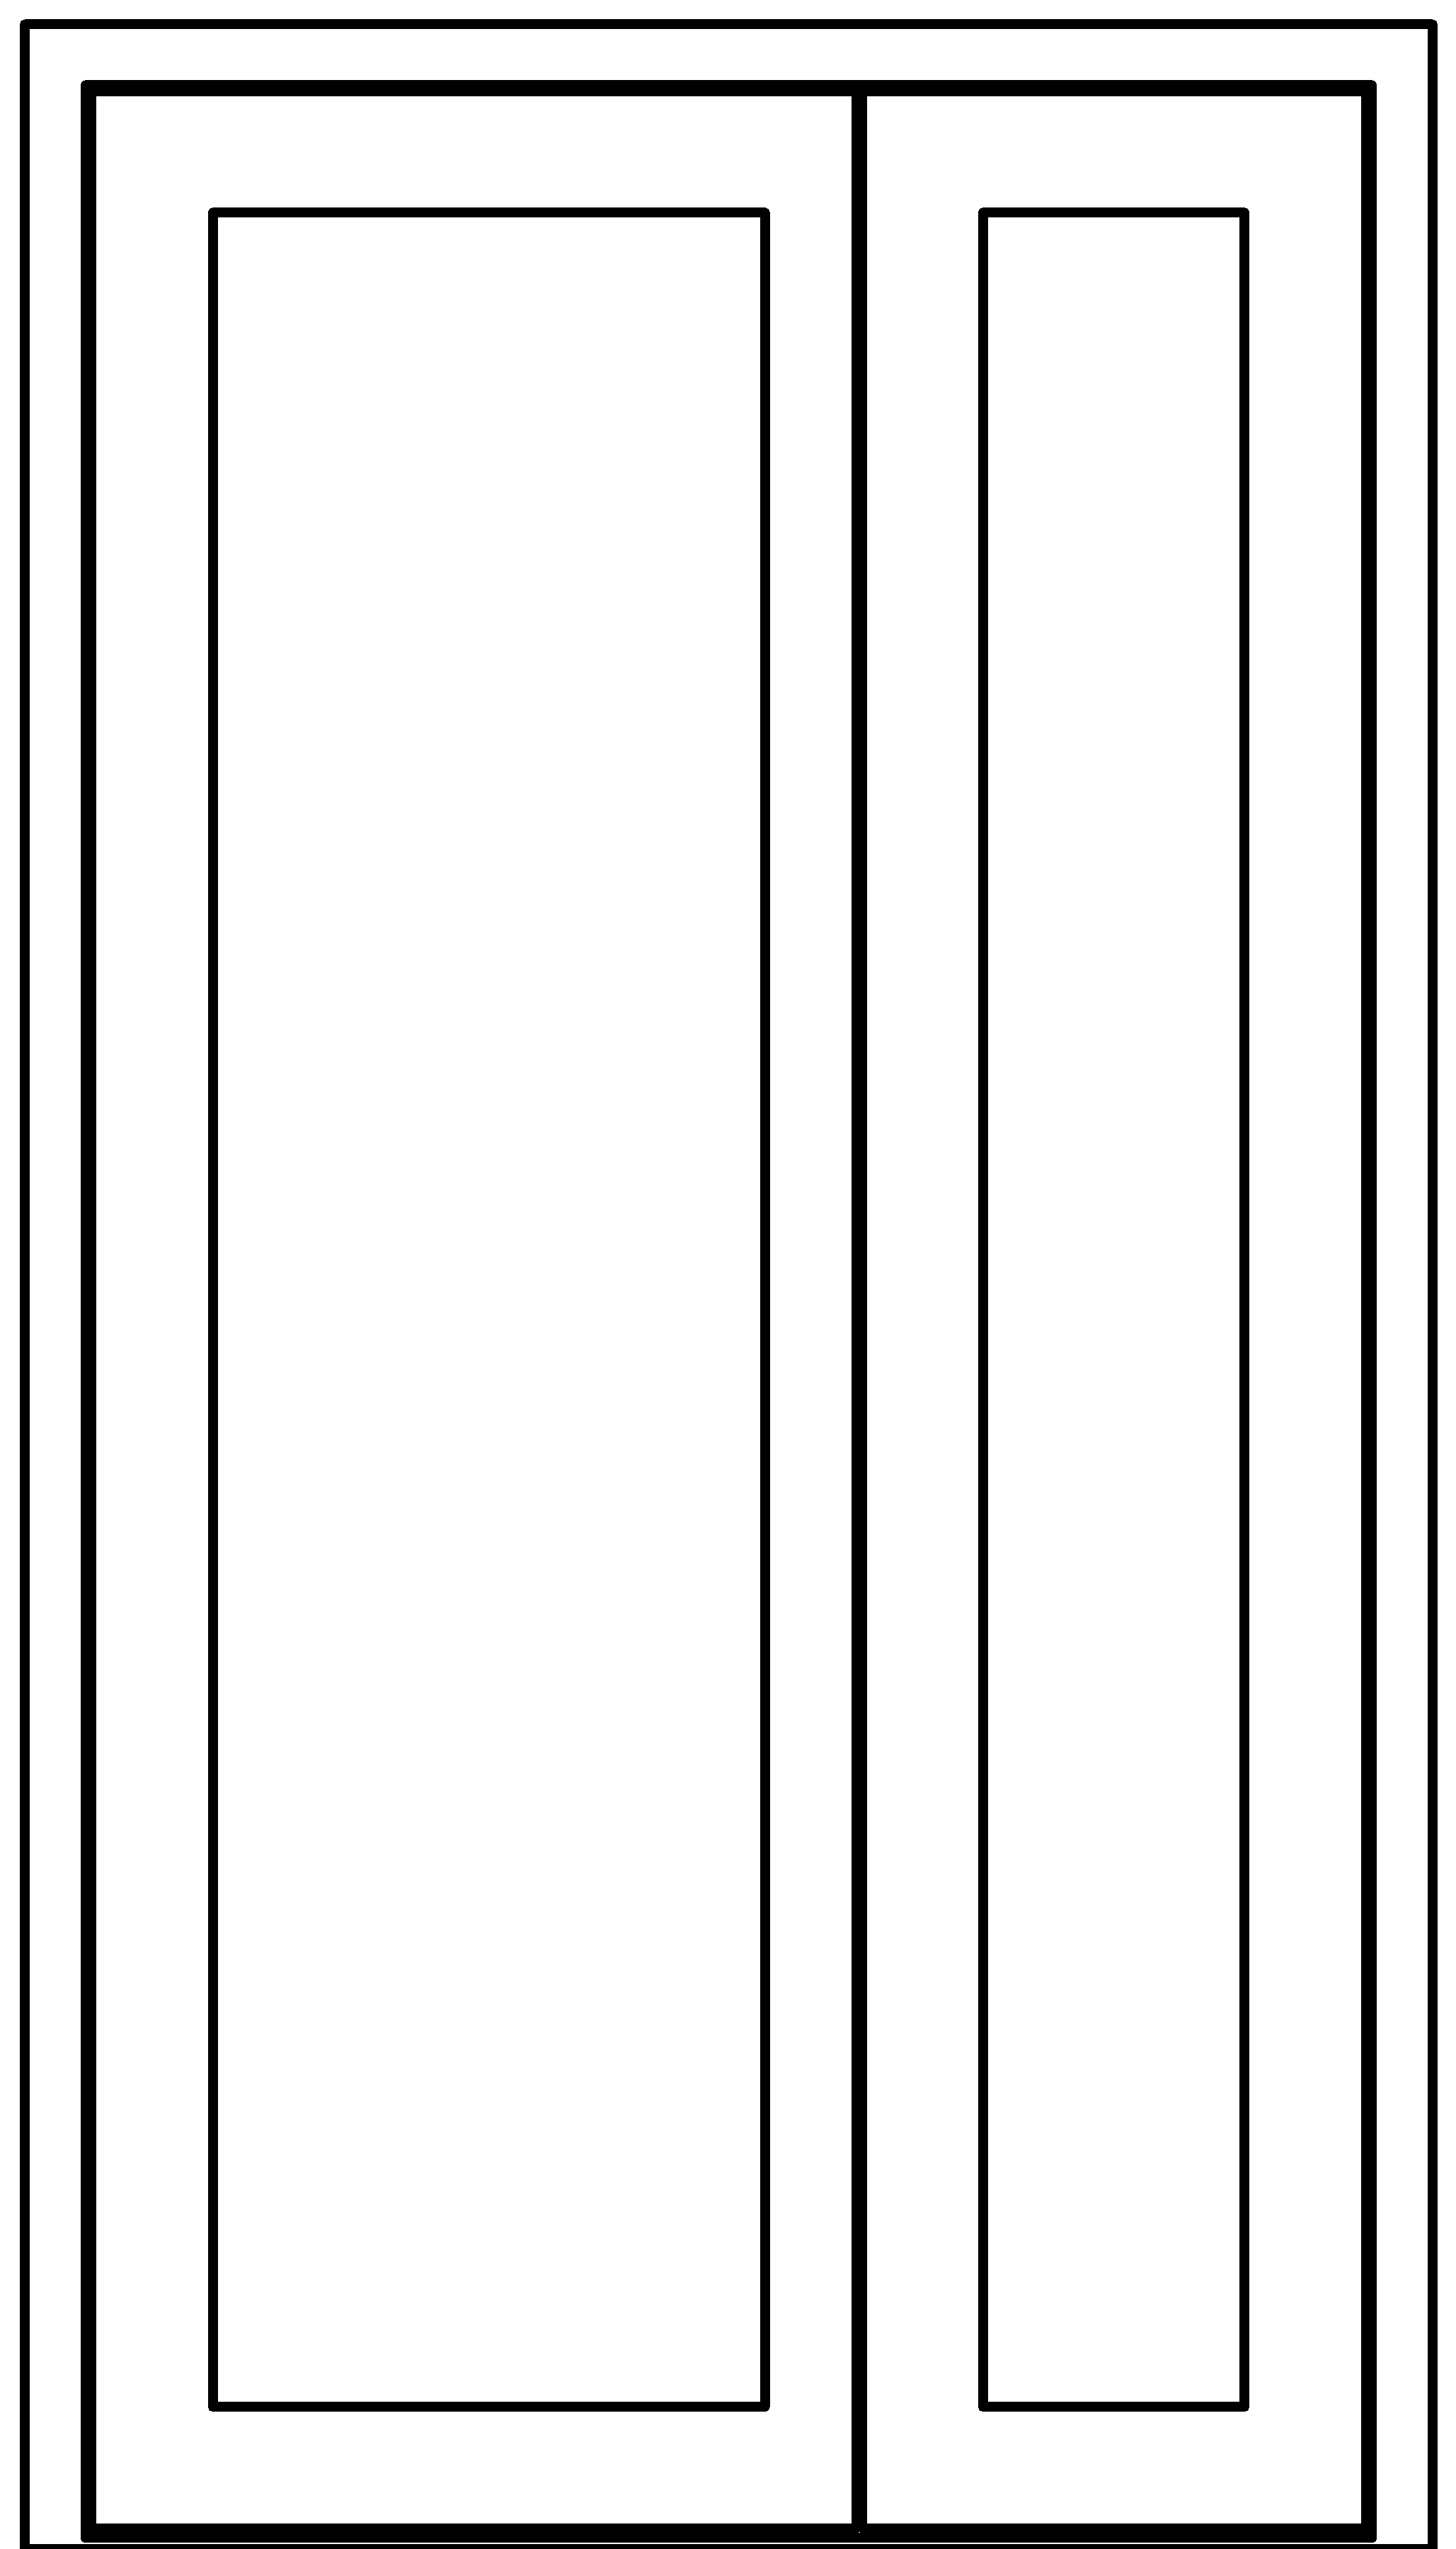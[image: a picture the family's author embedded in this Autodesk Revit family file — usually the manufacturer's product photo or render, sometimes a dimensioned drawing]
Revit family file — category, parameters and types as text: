
# Revit family: Дверь.Alumark_двупольная_S40
name_source: partatom
category: Двери
revit_build: Autodesk Revit 2017 (Build: 20171027_0315(x64)
units: mm (PartAtom-declared; Revit-internal decimal feet)

## family parameters
Всегда вертикально = Да
Заголовок OmniClass = Doors
Номер OmniClass = 23.30.10.00
Общий = Нет
Основа = Стена
При загрузке вырезать с полостями = Нет
Точка расчета площади = Нет

## types (2) — shared parameters
ADSK_Завод-изготовитель = ТБМ
ADSK_Обозначение = ГОСТ 23747-2015
URL = http://www.tbm.ru
sp_energy = Энергосберегающие стекла
sp_gaz = Заполненный газом
sp_standart = Обычный стеклопакет
Аналитическая конструкция = Застеклённая створчатая дверь, металлическая рама с двумя стеклами
Высота импоста = 800 мм
Дверь с цоколем = Нет
Заполнение стеклопакета = Обычный стеклопакет
Изготовитель = ТБМ
Изображение типоразмера = схема_двупольная_дверь.png
Импост двери = Нет
Коэффициент теплопередачи (U) = 4.2812 Вт/(м²·K)
Материал остекления = <По категории>
Материал профилей = <По категории>
Материал фурнитуры = <По категории>
Одинаковые полотна = Да
Описание = Дверь Проем ТБМ
Примерная высота = 2080 мм
Примерная ширина = 1160 мм
Разработчик = ООО ПРОРУБИМ
Разработчик (телефон) = +7(495)649-85-43
ТБМ_Артикул_Крепление порога = ALM740630
ТБМ_Артикул_Подкладка под СП = ALM740307
ТБМ_Артикул_Порог = ALM240391
ТБМ_Артикул_Рама = ALM240180
ТБМ_Артикул_Распорный штифт = ALM885014
ТБМ_Артикул_Т-соединитель рамы = ALM740322
ТБМ_Артикул_Угловой соединитель рамы = ALM740508
ТБМ_Артикул_Угловой соединитель створки = ALM740509
ТБМ_Артикул_Уголок выравнивающий = ALM740011
ТБМ_Артикул_Уплотнитель внутренний = 9GO/04
ТБМ_Артикул_Уплотнитель дверной декоративный = ELM0337
ТБМ_Артикул_Уплотнитель наружный = 9G0/42
ТБМ_Артикул_Уплотнитель порога = ELM0336
ТБМ_Артикул_Штапик = Р400/38
ТБМ_Длина_Порог = 1072 мм
ТБМ_Длина_Рама = 5320 мм
ТБМ_Длина_Створка = 8316 мм
ТБМ_Длина_Створка 2 = 2042 мм
ТБМ_Длина_Уплотнитель внутренний = 10358 мм
ТБМ_Длина_Уплотнитель дверной декоративный = 2042 мм
ТБМ_Длина_Уплотнитель наружный = 10358 мм
ТБМ_Длина_Уплотнитель порога = 1072 мм
ТБМ_Длина_Штапик = 9262 мм
ТБМ_Количество_Крепление порога = 1
ТБМ_Количество_Подкладка под СП = 8
ТБМ_Количество_Распорный штифт = 24
ТБМ_Количество_Т-соединитель рамы = 2
ТБМ_Количество_Угловой соединитель рамы = 4
ТБМ_Количество_Угловой соединитель створки = 8
ТБМ_Количество_Уголок выравнивающий = 6
ТБМ_Площадь стеклопакета = 1.56 м²
ТБМ_Стеклопакет_Высота 1 = 1882 мм
ТБМ_Стеклопакет_Высота 2 = 1882 мм
ТБМ_Стеклопакет_Ширина 1 = 414 мм
ТБМ_Стеклопакет_Ширина 2 = 414 мм
Термостойкость = 0.2336 (м²·K)/Вт
Тип стеклопакета = 24мм 1-камерный
Толщина = 40 мм
Функция = Наружные слои
Ширина створки слева = 460 мм
Ширина створки справа = 700 мм
импост_ширина = 53 мм
рама_ширина = 67 мм
сп_16_мм = 16мм 1-камерный
сп_24_мм = 24мм 1-камерный
створка_справа_ширина = 580 мм
створка_ширина = 81 мм
таблица выбора = каталог ТБМ двупольная дверь S44
штапик_толщина = 10 мм
zero-valued in all types: Коэффициент теплопритока от солнечного излучения, Пропускание видимого света, ТБМ_Длина_Импост, ТБМ_Длина_Цоколь, ТБМ_Количество_Т-соединитель цоколя

## per-type parameters (varying)
| type | ADSK_Наименование | Открывание внутрь | Открывание наружу | ТБМ_Артикул_Створка | ТБМ_Артикул_Створка 2 | номер профиля |
| 1160х2080 Открывание наружу (СП 24мм Обычный) | ДАН О Оп Р (Однокамерный стеклопакет 24 мм) | Нет | Да | ALM240281 | ALM240280 | 11101 |
| 1160х2080 Открывание внутрь (СП 24мм Обычный) | ДАВ О Оп Р (Однокамерный стеклопакет 24 мм) | Да | Нет | ALM240280 | ALM240281 | 21101 |
